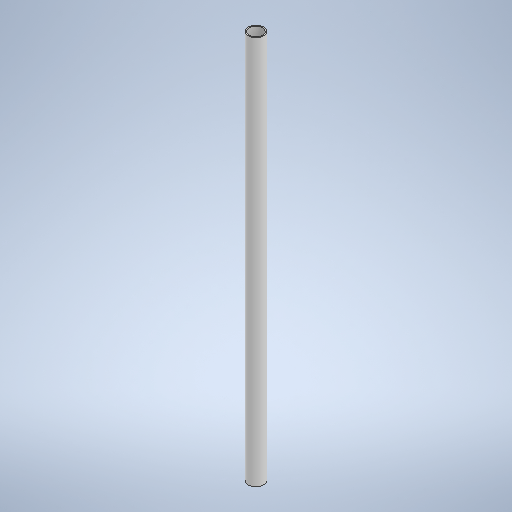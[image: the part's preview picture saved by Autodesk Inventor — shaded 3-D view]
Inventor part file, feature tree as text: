
AUTODESK INVENTOR PART (.ipt)
format: ipt  version: 2025.1 (Build 291241000, 241)  size: 236,032 bytes
history: native  units: mm
features: extrude x1, sketch x1
ambient origin geometry x8: Origin, YZ Plane, XZ Plane, XY Plane, X Axis, Y Axis, Z Axis, Center Point
bodies: Solide1 (feature_tree)
feature tree (2):
  extrude  "Extrusion1"  Depth=1.0mm
  sketch  "Esquisse1"
